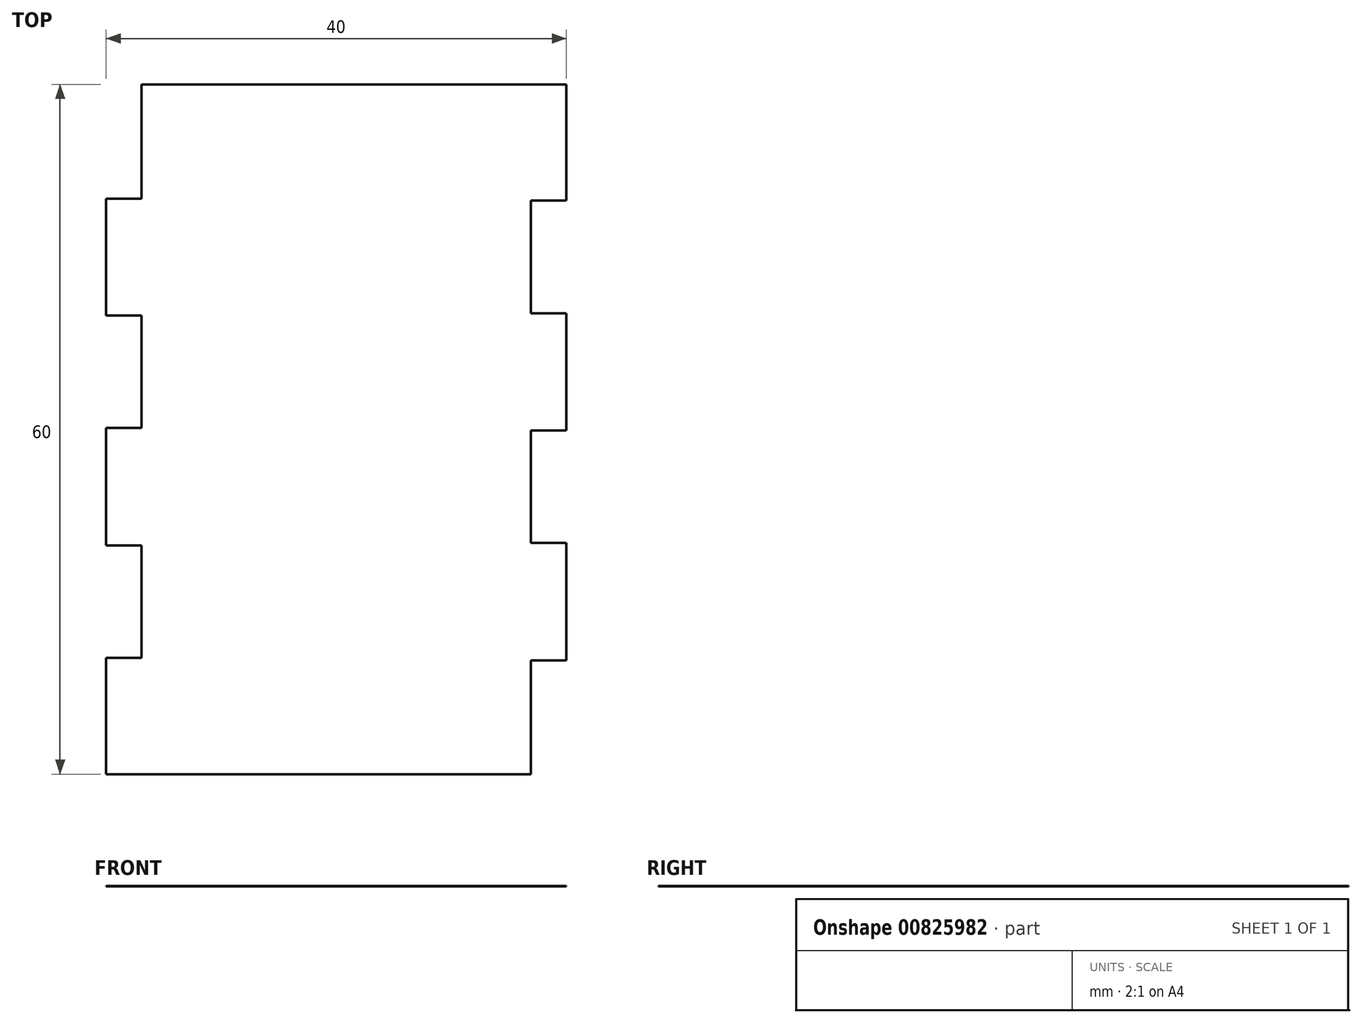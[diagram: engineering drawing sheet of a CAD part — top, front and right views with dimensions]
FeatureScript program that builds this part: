
annotation { "Feature Type Name" : "Feature", "Feature Type Description" : "" }
export const myFeature = defineFeature(function(context is Context, id is Id, definition is map)
    precondition{}
    {
        {
            var Q0;
            Q0=qCreatedBy(makeId("Top.planeOp"),FACE);
            var sketch = newSketch(context, id + "F0", { "sketchPlane" : qUnion([Q0])});
            skLineSegment(sketch, "E0.bottom", {"start": v(20, 30) * mm, "end": v(-20, 30) * mm});
            skLineSegment(sketch, "E0.top", {"start": v(20, -30) * mm, "end": v(-20, -30) * mm});
            skLineSegment(sketch, "E0.left", {"start": v(20, 30) * mm, "end": v(20, -30) * mm});
            skLineSegment(sketch, "E0.right", {"start": v(-20, 30) * mm, "end": v(-20, -30) * mm});
            skPoint(sketch, "E0.middle", {"position": v(0, 0) * mm});
            skSolve(sketch);
        }
        {
            var Q0;
            Q0 = qSketchRegion(id + "F0", true);
            extrude(context, id + "F1", {"entities" : qUnion([Q0]), "depth" : 1 / 203.2 * mm, "offsetDistance" : 25 * mm});
        }
        {
            var Q0;
            Q0=makeQuery(id+"F1.opExtrude","CAP_FACE",FACE,{"disambiguationData":[OSD([sQuery(id+"F0.wireOp",EDGE,"E0.bottom"),sQuery(id+"F0.wireOp",EDGE,"E0.top"),sQuery(id+"F0.wireOp",EDGE,"E0.left"),sQuery(id+"F0.wireOp",EDGE,"E0.right")])],"isStart":false});
            var sketch = newSketch(context, id + "F2", { "sketchPlane" : qUnion([Q0])});
            skLineSegment(sketch, "E1", {"start": v(20, -30) * mm, "end": v(16.93, -30) * mm, "construction": true});
            skLineSegment(sketch, "E2", {"start": v(16.92, -30) * mm, "end": v(16.92, 30) * mm, "construction": true});
            skLineSegment(sketch, "E3.0.1.0", {"start": v(20, -20) * mm, "end": v(16.93, -20) * mm, "construction": true});
            skLineSegment(sketch, "E3.0.2.0", {"start": v(20, -10) * mm, "end": v(16.93, -10) * mm, "construction": true});
            skLineSegment(sketch, "E3.0.3.0", {"start": v(20, 0) * mm, "end": v(16.93, 0) * mm, "construction": true});
            skLineSegment(sketch, "E3.0.4.0", {"start": v(20, 10) * mm, "end": v(16.93, 10) * mm, "construction": true});
            skLineSegment(sketch, "E3.0.5.0", {"start": v(20, 20) * mm, "end": v(16.93, 20) * mm, "construction": true});
            skLineSegment(sketch, "E3.direction1", {"start": v(16.93, -30) * mm, "end": v(20, -30) * mm, "construction": true});
            skLineSegment(sketch, "E3.direction2", {"start": v(16.93, -30) * mm, "end": v(16.93, -20) * mm, "construction": true});
            skLineSegment(sketch, "E4.MirrorCS", {"start": v(-20, -30) * mm, "end": v(-16.93, -30) * mm, "construction": true});
            skLineSegment(sketch, "E5.MirrorCS", {"start": v(-16.93, -30) * mm, "end": v(-20, -30) * mm, "construction": true});
            skLineSegment(sketch, "E6.MirrorCS", {"start": v(-20, -20) * mm, "end": v(-16.93, -20) * mm, "construction": true});
            skLineSegment(sketch, "E7.MirrorCS", {"start": v(-20, 10) * mm, "end": v(-16.93, 10) * mm, "construction": true});
            skLineSegment(sketch, "E8.MirrorCS", {"start": v(-20, -10) * mm, "end": v(-16.93, -10) * mm, "construction": true});
            skLineSegment(sketch, "E9.MirrorCS", {"start": v(-20, 20) * mm, "end": v(-16.93, 20) * mm, "construction": true});
            skLineSegment(sketch, "E10.MirrorCS", {"start": v(-20, 0) * mm, "end": v(-16.93, 0) * mm, "construction": true});
            skLineSegment(sketch, "E11.MirrorCS", {"start": v(-16.93, -30) * mm, "end": v(-16.93, -20) * mm, "construction": true});
            skLineSegment(sketch, "E12.MirrorCS", {"start": v(-16.93, -30) * mm, "end": v(-16.93, 30) * mm, "construction": true});
            skLineSegment(sketch, "E13", {"start": v(16.93, -30) * mm, "end": v(16.93, -20.1) * mm});
            skLineSegment(sketch, "E14", {"start": v(16.93, -20.1) * mm, "end": v(20, -20.1) * mm});
            skLineSegment(sketch, "E15", {"start": v(20, -20.1) * mm, "end": v(20, -9.9) * mm});
            skLineSegment(sketch, "E16", {"start": v(20, -9.9) * mm, "end": v(16.92, -9.9) * mm});
            skLineSegment(sketch, "E17", {"start": v(16.92, -9.9) * mm, "end": v(16.92, -0.1) * mm});
            skLineSegment(sketch, "E18", {"start": v(16.92, -0.1) * mm, "end": v(20, -0.1) * mm});
            skLineSegment(sketch, "E19", {"start": v(20, -0.1) * mm, "end": v(20, 10.1) * mm});
            skLineSegment(sketch, "E20", {"start": v(20, 10.1) * mm, "end": v(16.92, 10.1) * mm});
            skLineSegment(sketch, "E21", {"start": v(16.92, 10.1) * mm, "end": v(16.92, 19.9) * mm});
            skLineSegment(sketch, "E22", {"start": v(16.92, 19.9) * mm, "end": v(20, 19.9) * mm});
            skLineSegment(sketch, "E23", {"start": v(20, 19.9) * mm, "end": v(20, 30) * mm});
            skLineSegment(sketch, "E24", {"start": v(-20, -30) * mm, "end": v(-20, -19.9) * mm});
            skLineSegment(sketch, "E25", {"start": v(-20, -19.9) * mm, "end": v(-16.93, -19.9) * mm});
            skLineSegment(sketch, "E26", {"start": v(-16.93, -19.9) * mm, "end": v(-16.93, -10.1) * mm});
            skLineSegment(sketch, "E27", {"start": v(-16.93, -10.1) * mm, "end": v(-20, -10.1) * mm});
            skLineSegment(sketch, "E28", {"start": v(-20, -10.1) * mm, "end": v(-20, 0.1) * mm});
            skLineSegment(sketch, "E29", {"start": v(-20, 0.1) * mm, "end": v(-16.93, 0.1) * mm});
            skLineSegment(sketch, "E30", {"start": v(-16.93, 0.1) * mm, "end": v(-16.93, 9.9) * mm});
            skLineSegment(sketch, "E31", {"start": v(-16.93, 9.9) * mm, "end": v(-20, 9.9) * mm});
            skLineSegment(sketch, "E32", {"start": v(-20, 9.9) * mm, "end": v(-20, 20.05) * mm});
            skLineSegment(sketch, "E33", {"start": v(-20, 20.05) * mm, "end": v(-16.93, 20.05) * mm});
            skLineSegment(sketch, "E34", {"start": v(-16.93, 20.05) * mm, "end": v(-16.93, 30) * mm});
            skSolve(sketch);
        }
        {
            var Q0;
            {var subQ0=sQuery(id+"F2.wireOp",EDGE,"E13");Q0=makeQuery(id+"F2.imprint","IMPRINT",FACE,{"disambiguationData":[TD([[makeQuery(id+"F2.imprint","IMPRINT",EDGE,{"derivedFrom":subQ0}),-1.0]])]});}
            var Q1;
            {var subQ0=sQuery(id+"F2.wireOp",EDGE,"E16");Q1=makeQuery(id+"F2.imprint","IMPRINT",FACE,{"disambiguationData":[TD([[makeQuery(id+"F2.imprint","IMPRINT",EDGE,{"derivedFrom":subQ0}),-1.0]])]});}
            var Q2;
            {var subQ0=sQuery(id+"F2.wireOp",EDGE,"E20");Q2=makeQuery(id+"F2.imprint","IMPRINT",FACE,{"disambiguationData":[TD([[makeQuery(id+"F2.imprint","IMPRINT",EDGE,{"derivedFrom":subQ0}),-1.0]])]});}
            var Q3;
            {var subQ0=sQuery(id+"F2.wireOp",EDGE,"E25");Q3=makeQuery(id+"F2.imprint","IMPRINT",FACE,{"disambiguationData":[TD([[makeQuery(id+"F2.imprint","IMPRINT",EDGE,{"derivedFrom":subQ0}),1.0]])]});}
            var Q4;
            {var subQ0=sQuery(id+"F2.wireOp",EDGE,"E29");Q4=makeQuery(id+"F2.imprint","IMPRINT",FACE,{"disambiguationData":[TD([[makeQuery(id+"F2.imprint","IMPRINT",EDGE,{"derivedFrom":subQ0}),1.0]])]});}
            var Q5;
            {var subQ0=sQuery(id+"F2.wireOp",EDGE,"E33");Q5=makeQuery(id+"F2.imprint","IMPRINT",FACE,{"disambiguationData":[TD([[makeQuery(id+"F2.imprint","IMPRINT",EDGE,{"derivedFrom":subQ0}),1.0]])]});}
            extrude(context, id + "F3", {"entities" : qUnion([Q0, Q1, Q2, Q3, Q4, Q5]), "operationType" : NewBodyOperationType.REMOVE, "oppositeDirection" : true, "depth" : 25 * mm, "offsetDistance" : 25 * mm});
        }
    });
